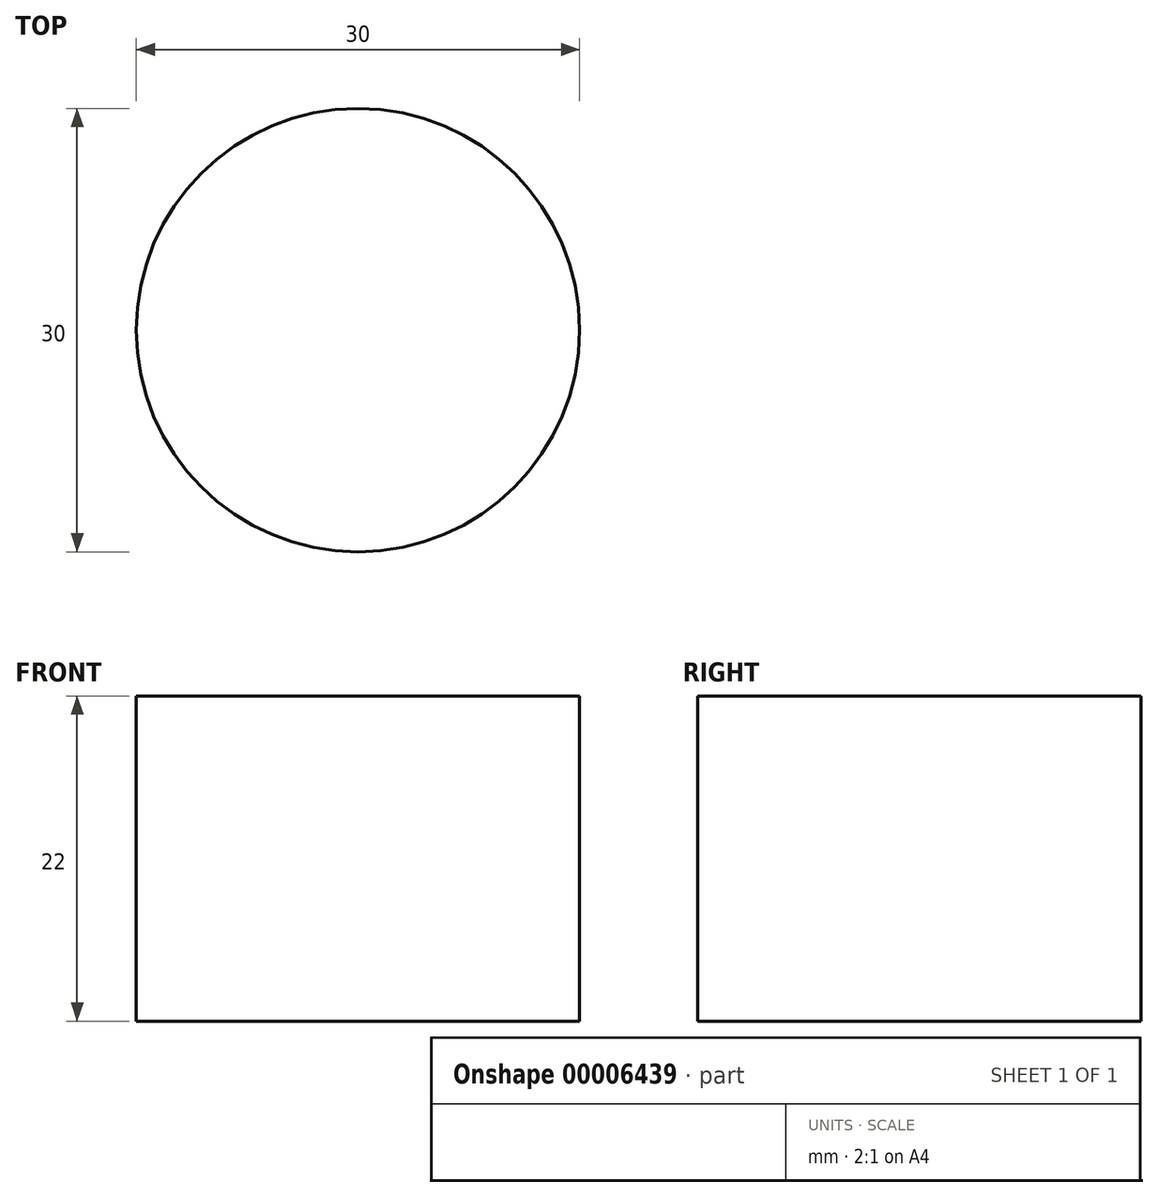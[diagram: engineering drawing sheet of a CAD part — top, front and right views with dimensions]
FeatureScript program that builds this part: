
annotation { "Feature Type Name" : "Feature", "Feature Type Description" : "" }
export const myFeature = defineFeature(function(context is Context, id is Id, definition is map)
    precondition{}
    {
        {
            var Q0;
            Q0=qCreatedBy(makeId("Top.planeOp"),FACE);
            var sketch = newSketch(context, id + "F0", { "sketchPlane" : qUnion([Q0])});
            skCircle(sketch, "E0", {"center": v(0, 0) * mm, "radius": 15 * mm});
            skSolve(sketch);
        }
        {
            var Q0;
            Q0=makeQuery(id+"F0.imprint","IMPRINT",FACE,{"disambiguationData":[TD([[makeQuery(id+"F0.imprint","IMPRINT",EDGE,{"derivedFrom":sQuery(id+"F0.wireOp",EDGE,"E0")}),1.0]])]});
            extrude(context, id + "F1", {"entities" : qUnion([Q0]), "depth" : 22 * mm});
        }
    });
